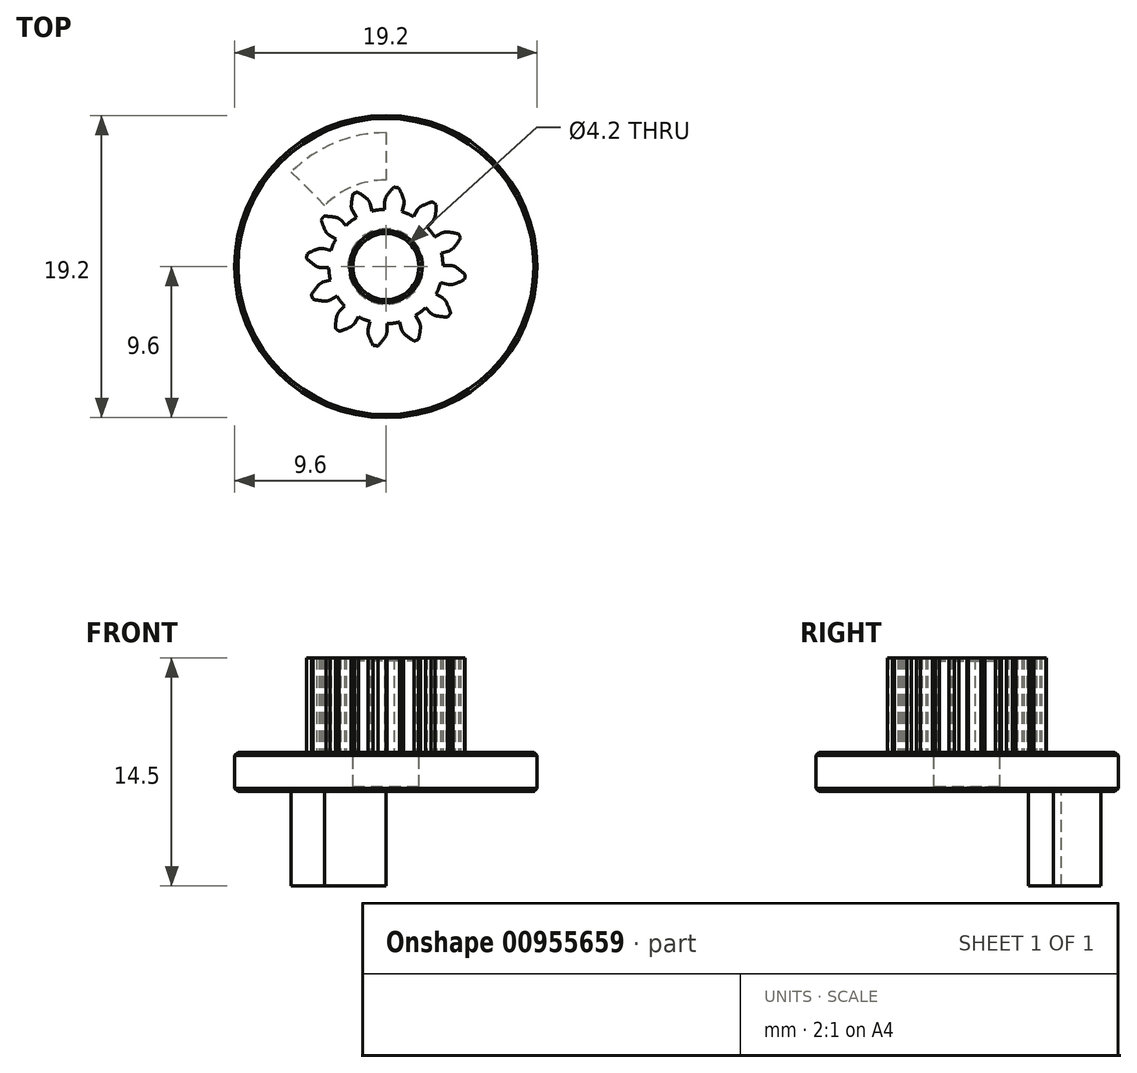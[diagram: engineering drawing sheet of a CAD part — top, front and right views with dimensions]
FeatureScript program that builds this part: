
annotation { "Feature Type Name" : "Feature", "Feature Type Description" : "" }
export const myFeature = defineFeature(function(context is Context, id is Id, definition is map)
    precondition{}
    {
        {
            var Q0;
            Q0=qCreatedBy(makeId("Top.planeOp"),FACE);
            var sketch = newSketch(context, id + "F0", { "sketchPlane" : qUnion([Q0])});
            skCircle(sketch, "E0", {"center": v(0, 0) * mm, "radius": 9.6 * mm});
            skCircle(sketch, "E1", {"center": v(0, 0) * mm, "radius": 2.1 * mm});
            skSolve(sketch);
        }
        {
            var Q0;
            Q0 = qSketchRegion(id + "F0", true);
            extrude(context, id + "F1", {"entities" : qUnion([Q0]), "oppositeDirection" : true, "depth" : 2.5 * mm, "offsetDistance" : 25 * mm});
        }
        {
            var Q0;
            Q0=makeQuery(id+"F1.opExtrude","CAP_FACE",FACE,{"disambiguationData":[OSD([sQuery(id+"F0.wireOp",EDGE,"E0"),sQuery(id+"F0.wireOp",EDGE,"E1")])],"isStart":false});
            var sketch = newSketch(context, id + "F2", { "sketchPlane" : qUnion([Q0])});
            skArc(sketch, "E2", {"start": v(-6.01, -6.01) * mm, "mid": v(-3.25, -7.85) * mm, "end": v(0, -8.5) * mm});
            skArc(sketch, "E3", {"start": v(-3.89, -3.89) * mm, "mid": v(-2.1, -5.08) * mm, "end": v(0, -5.5) * mm});
            skLineSegment(sketch, "E4", {"start": v(0, -8.5) * mm, "end": v(0, -5.5) * mm});
            skLineSegment(sketch, "E5", {"start": v(-6.01, -6.01) * mm, "end": v(-3.89, -3.89) * mm});
            skSolve(sketch);
        }
        {
            var Q0;
            Q0 = qSketchRegion(id + "F2", true);
            extrude(context, id + "F3", {"entities" : qUnion([Q0]), "operationType" : NewBodyOperationType.ADD, "depth" : 6 * mm, "offsetDistance" : 25 * mm});
        }
        {
            var Q0;
            Q0=makeQuery(id+"F1.opExtrude","CAP_FACE",FACE,{"disambiguationData":[OSD([sQuery(id+"F0.wireOp",EDGE,"E0"),sQuery(id+"F0.wireOp",EDGE,"E1")])],"isStart":true});
            var sketch = newSketch(context, id + "F4", { "sketchPlane" : qUnion([Q0])});
            skCircle(sketch, "E6", {"center": v(0, 0) * mm, "radius": 4.4 * mm, "construction": true});
            skLineSegment(sketch, "E7", {"start": v(0, 0) * mm, "end": v(0, 9.6) * mm, "construction": true});
            skLineSegment(sketch, "E8", {"start": v(-3.58, 4.4) * mm, "end": v(3.94, 4.4) * mm, "construction": true});
            skPoint(sketch, "E9", {"position": v(0, 4.4) * mm});
            skLineSegment(sketch, "E10", {"start": v(-4.04, 2.93) * mm, "end": v(3.69, 5.74) * mm, "construction": true});
            skLineSegment(sketch, "E11", {"start": v(0, 0) * mm, "end": v(-1.41, 3.89) * mm, "construction": true});
            skCircle(sketch, "E12", {"center": v(0, 0) * mm, "radius": 4.13 * mm, "construction": true});
            skArc(sketch, "E13", {"start": v(-3.93, 3.2) * mm, "mid": v(-4.02, 3.08) * mm, "end": v(-4.1, 2.96) * mm});
            skCircle(sketch, "E14", {"center": v(0, 0) * mm, "radius": 3.63 * mm});
            skPoint(sketch, "E15", {"position": v(3.58, 2.06) * mm});
            skPoint(sketch, "E16", {"position": v(1.64, 3.8) * mm});
            skArc(sketch, "E17", {"start": v(0, 4.4) * mm, "mid": v(0.24, 4.73) * mm, "end": v(0.51, 5.04) * mm});
            skArc(sketch, "E18", {"start": v(0, 4.4) * mm, "mid": v(-0.04, 4.27) * mm, "end": v(-0.07, 4.13) * mm});
            skLineSegment(sketch, "E19", {"start": v(-0.07, 4.13) * mm, "end": v(-0.07, 3.63) * mm});
            skLineSegment(sketch, "E20", {"start": v(0, 0) * mm, "end": v(0.83, 6.34) * mm, "construction": true});
            skLineSegment(sketch, "E21.MirrorCS", {"start": v(1.14, 3.97) * mm, "end": v(1.01, 3.48) * mm});
            skArc(sketch, "E22.MirrorCS", {"start": v(1.14, 4.25) * mm, "mid": v(1.15, 4.11) * mm, "end": v(1.14, 3.97) * mm});
            skArc(sketch, "E23.MirrorCS", {"start": v(1.14, 4.25) * mm, "mid": v(1, 4.63) * mm, "end": v(0.81, 5) * mm});
            skArc(sketch, "E24.1.0", {"start": v(-2.2, 3.81) * mm, "mid": v(-2.16, 4.22) * mm, "end": v(-2.08, 4.62) * mm});
            skArc(sketch, "E24.1.1", {"start": v(-2.2, 3.81) * mm, "mid": v(-2.17, 3.68) * mm, "end": v(-2.13, 3.54) * mm});
            skLineSegment(sketch, "E24.1.2", {"start": v(-2.13, 3.54) * mm, "end": v(-1.88, 3.1) * mm});
            skLineSegment(sketch, "E24.1.3", {"start": v(-1, 4.01) * mm, "end": v(-0.87, 3.52) * mm});
            skArc(sketch, "E24.1.4", {"start": v(-1.14, 4.25) * mm, "mid": v(-1.06, 4.13) * mm, "end": v(-1, 4.01) * mm});
            skArc(sketch, "E24.1.5", {"start": v(-1.14, 4.25) * mm, "mid": v(-1.46, 4.5) * mm, "end": v(-1.8, 4.74) * mm});
            skArc(sketch, "E24.2.0", {"start": v(-3.81, 2.2) * mm, "mid": v(-3.98, 2.57) * mm, "end": v(-4.1, 2.96) * mm});
            skArc(sketch, "E24.2.1", {"start": v(-3.81, 2.2) * mm, "mid": v(-3.72, 2.1) * mm, "end": v(-3.62, 2) * mm});
            skLineSegment(sketch, "E24.2.2", {"start": v(-3.62, 2) * mm, "end": v(-3.18, 1.75) * mm});
            skLineSegment(sketch, "E24.2.3", {"start": v(-2.87, 2.98) * mm, "end": v(-2.51, 2.62) * mm});
            skArc(sketch, "E24.2.4", {"start": v(-3.11, 3.11) * mm, "mid": v(-2.99, 3.05) * mm, "end": v(-2.87, 2.98) * mm});
            skArc(sketch, "E24.2.5", {"start": v(-3.11, 3.11) * mm, "mid": v(-3.52, 3.18) * mm, "end": v(-3.93, 3.2) * mm});
            skArc(sketch, "E24.3.0", {"start": v(-4.4, 0) * mm, "mid": v(-4.73, 0.24) * mm, "end": v(-5.04, 0.51) * mm});
            skArc(sketch, "E24.3.1", {"start": v(-4.4, 0) * mm, "mid": v(-4.27, -0.04) * mm, "end": v(-4.13, -0.07) * mm});
            skLineSegment(sketch, "E24.3.2", {"start": v(-4.13, -0.07) * mm, "end": v(-3.63, -0.07) * mm});
            skLineSegment(sketch, "E24.3.3", {"start": v(-3.97, 1.14) * mm, "end": v(-3.48, 1.01) * mm});
            skArc(sketch, "E24.3.4", {"start": v(-4.25, 1.14) * mm, "mid": v(-4.11, 1.15) * mm, "end": v(-3.97, 1.14) * mm});
            skArc(sketch, "E24.3.5", {"start": v(-4.25, 1.14) * mm, "mid": v(-4.63, 1) * mm, "end": v(-5, 0.81) * mm});
            skArc(sketch, "E24.4.0", {"start": v(-3.81, -2.2) * mm, "mid": v(-4.22, -2.16) * mm, "end": v(-4.62, -2.08) * mm});
            skArc(sketch, "E24.4.1", {"start": v(-3.81, -2.2) * mm, "mid": v(-3.68, -2.17) * mm, "end": v(-3.54, -2.13) * mm});
            skLineSegment(sketch, "E24.4.2", {"start": v(-3.54, -2.13) * mm, "end": v(-3.1, -1.88) * mm});
            skLineSegment(sketch, "E24.4.3", {"start": v(-4.01, -1) * mm, "end": v(-3.52, -0.87) * mm});
            skArc(sketch, "E24.4.4", {"start": v(-4.25, -1.14) * mm, "mid": v(-4.13, -1.06) * mm, "end": v(-4.01, -1) * mm});
            skArc(sketch, "E24.4.5", {"start": v(-4.25, -1.14) * mm, "mid": v(-4.5, -1.46) * mm, "end": v(-4.74, -1.8) * mm});
            skArc(sketch, "E24.5.0", {"start": v(-2.2, -3.81) * mm, "mid": v(-2.57, -3.98) * mm, "end": v(-2.96, -4.1) * mm});
            skArc(sketch, "E24.5.1", {"start": v(-2.2, -3.81) * mm, "mid": v(-2.1, -3.72) * mm, "end": v(-2, -3.62) * mm});
            skLineSegment(sketch, "E24.5.2", {"start": v(-2, -3.62) * mm, "end": v(-1.75, -3.18) * mm});
            skLineSegment(sketch, "E24.5.3", {"start": v(-2.98, -2.87) * mm, "end": v(-2.62, -2.51) * mm});
            skArc(sketch, "E24.5.4", {"start": v(-3.11, -3.11) * mm, "mid": v(-3.05, -2.99) * mm, "end": v(-2.98, -2.87) * mm});
            skArc(sketch, "E24.5.5", {"start": v(-3.11, -3.11) * mm, "mid": v(-3.18, -3.52) * mm, "end": v(-3.2, -3.93) * mm});
            skArc(sketch, "E24.6.0", {"start": v(0, -4.4) * mm, "mid": v(-0.24, -4.73) * mm, "end": v(-0.51, -5.04) * mm});
            skArc(sketch, "E24.6.1", {"start": v(0, -4.4) * mm, "mid": v(0.04, -4.27) * mm, "end": v(0.07, -4.13) * mm});
            skLineSegment(sketch, "E24.6.2", {"start": v(0.07, -4.13) * mm, "end": v(0.07, -3.63) * mm});
            skLineSegment(sketch, "E24.6.3", {"start": v(-1.14, -3.97) * mm, "end": v(-1.01, -3.48) * mm});
            skArc(sketch, "E24.6.4", {"start": v(-1.14, -4.25) * mm, "mid": v(-1.15, -4.11) * mm, "end": v(-1.14, -3.97) * mm});
            skArc(sketch, "E24.6.5", {"start": v(-1.14, -4.25) * mm, "mid": v(-1, -4.63) * mm, "end": v(-0.81, -5) * mm});
            skArc(sketch, "E24.7.0", {"start": v(2.2, -3.81) * mm, "mid": v(2.16, -4.22) * mm, "end": v(2.08, -4.62) * mm});
            skArc(sketch, "E24.7.1", {"start": v(2.2, -3.81) * mm, "mid": v(2.17, -3.68) * mm, "end": v(2.13, -3.54) * mm});
            skLineSegment(sketch, "E24.7.2", {"start": v(2.13, -3.54) * mm, "end": v(1.88, -3.1) * mm});
            skLineSegment(sketch, "E24.7.3", {"start": v(1, -4.01) * mm, "end": v(0.87, -3.52) * mm});
            skArc(sketch, "E24.7.4", {"start": v(1.14, -4.25) * mm, "mid": v(1.06, -4.13) * mm, "end": v(1, -4.01) * mm});
            skArc(sketch, "E24.7.5", {"start": v(1.14, -4.25) * mm, "mid": v(1.46, -4.5) * mm, "end": v(1.8, -4.74) * mm});
            skArc(sketch, "E24.8.0", {"start": v(3.81, -2.2) * mm, "mid": v(3.98, -2.57) * mm, "end": v(4.1, -2.96) * mm});
            skArc(sketch, "E24.8.1", {"start": v(3.81, -2.2) * mm, "mid": v(3.72, -2.1) * mm, "end": v(3.62, -2) * mm});
            skLineSegment(sketch, "E24.8.2", {"start": v(3.62, -2) * mm, "end": v(3.18, -1.75) * mm});
            skLineSegment(sketch, "E24.8.3", {"start": v(2.87, -2.98) * mm, "end": v(2.51, -2.62) * mm});
            skArc(sketch, "E24.8.4", {"start": v(3.11, -3.11) * mm, "mid": v(2.99, -3.05) * mm, "end": v(2.87, -2.98) * mm});
            skArc(sketch, "E24.8.5", {"start": v(3.11, -3.11) * mm, "mid": v(3.52, -3.18) * mm, "end": v(3.93, -3.2) * mm});
            skArc(sketch, "E24.9.0", {"start": v(4.4, 0) * mm, "mid": v(4.73, -0.24) * mm, "end": v(5.04, -0.51) * mm});
            skArc(sketch, "E24.9.1", {"start": v(4.4, 0) * mm, "mid": v(4.27, 0.04) * mm, "end": v(4.13, 0.07) * mm});
            skLineSegment(sketch, "E24.9.2", {"start": v(4.13, 0.07) * mm, "end": v(3.63, 0.07) * mm});
            skLineSegment(sketch, "E24.9.3", {"start": v(3.97, -1.14) * mm, "end": v(3.48, -1.01) * mm});
            skArc(sketch, "E24.9.4", {"start": v(4.25, -1.14) * mm, "mid": v(4.11, -1.15) * mm, "end": v(3.97, -1.14) * mm});
            skArc(sketch, "E24.9.5", {"start": v(4.25, -1.14) * mm, "mid": v(4.63, -1) * mm, "end": v(5, -0.81) * mm});
            skArc(sketch, "E24.10.0", {"start": v(3.81, 2.2) * mm, "mid": v(4.22, 2.16) * mm, "end": v(4.62, 2.08) * mm});
            skArc(sketch, "E24.10.1", {"start": v(3.81, 2.2) * mm, "mid": v(3.68, 2.17) * mm, "end": v(3.54, 2.13) * mm});
            skLineSegment(sketch, "E24.10.2", {"start": v(3.54, 2.13) * mm, "end": v(3.1, 1.88) * mm});
            skLineSegment(sketch, "E24.10.3", {"start": v(4.01, 1) * mm, "end": v(3.52, 0.87) * mm});
            skArc(sketch, "E24.10.4", {"start": v(4.25, 1.14) * mm, "mid": v(4.13, 1.06) * mm, "end": v(4.01, 1) * mm});
            skArc(sketch, "E24.10.5", {"start": v(4.25, 1.14) * mm, "mid": v(4.5, 1.46) * mm, "end": v(4.74, 1.8) * mm});
            skArc(sketch, "E24.11.0", {"start": v(2.2, 3.81) * mm, "mid": v(2.57, 3.98) * mm, "end": v(2.96, 4.1) * mm});
            skArc(sketch, "E24.11.1", {"start": v(2.2, 3.81) * mm, "mid": v(2.1, 3.72) * mm, "end": v(2, 3.62) * mm});
            skLineSegment(sketch, "E24.11.2", {"start": v(2, 3.62) * mm, "end": v(1.75, 3.18) * mm});
            skLineSegment(sketch, "E24.11.3", {"start": v(2.98, 2.87) * mm, "end": v(2.62, 2.51) * mm});
            skArc(sketch, "E24.11.4", {"start": v(3.11, 3.11) * mm, "mid": v(3.05, 2.99) * mm, "end": v(2.98, 2.87) * mm});
            skArc(sketch, "E24.11.5", {"start": v(3.11, 3.11) * mm, "mid": v(3.18, 3.52) * mm, "end": v(3.2, 3.93) * mm});
            skArc(sketch, "E25.trimOffspring", {"start": v(-5, 0.81) * mm, "mid": v(-5.02, 0.66) * mm, "end": v(-5.04, 0.51) * mm});
            skArc(sketch, "E26.trimOffspring", {"start": v(-4.74, -1.8) * mm, "mid": v(-4.68, -1.94) * mm, "end": v(-4.62, -2.08) * mm});
            skArc(sketch, "E27.trimOffspring", {"start": v(-3.2, -3.93) * mm, "mid": v(-3.08, -4.02) * mm, "end": v(-2.96, -4.1) * mm});
            skArc(sketch, "E28.trimOffspring", {"start": v(-0.81, -5) * mm, "mid": v(-0.66, -5.02) * mm, "end": v(-0.51, -5.04) * mm});
            skArc(sketch, "E29.trimOffspring", {"start": v(1.8, -4.74) * mm, "mid": v(1.94, -4.68) * mm, "end": v(2.08, -4.62) * mm});
            skArc(sketch, "E30.trimOffspring", {"start": v(3.93, -3.2) * mm, "mid": v(4.02, -3.08) * mm, "end": v(4.1, -2.96) * mm});
            skArc(sketch, "E31.trimOffspring", {"start": v(5, -0.81) * mm, "mid": v(5.02, -0.66) * mm, "end": v(5.04, -0.51) * mm});
            skArc(sketch, "E32.trimOffspring", {"start": v(4.74, 1.8) * mm, "mid": v(4.68, 1.94) * mm, "end": v(4.62, 2.08) * mm});
            skArc(sketch, "E33.trimOffspring", {"start": v(3.2, 3.93) * mm, "mid": v(3.08, 4.02) * mm, "end": v(2.96, 4.1) * mm});
            skArc(sketch, "E34.trimOffspring", {"start": v(0.81, 5) * mm, "mid": v(0.66, 5.02) * mm, "end": v(0.51, 5.04) * mm});
            skArc(sketch, "E35.trimOffspring", {"start": v(-1.8, 4.74) * mm, "mid": v(-1.94, 4.68) * mm, "end": v(-2.08, 4.62) * mm});
            skCircle(sketch, "E36", {"center": v(0, 0) * mm, "radius": 2.1 * mm});
            skSolve(sketch);
        }
        {
            var Q0;
            Q0 = qSketchRegion(id + "F4", true);
            extrude(context, id + "F5", {"entities" : qUnion([Q0]), "operationType" : NewBodyOperationType.ADD, "depth" : 6 * mm, "offsetDistance" : 25 * mm});
        }
        {
            var Q0;
            Q0=makeQuery(id+"F1.opExtrude","CAP_EDGE",EDGE,{"disambiguationData":[OSD([sQuery(id+"F0.wireOp",EDGE,"E1")])],"isStart":false});
            chamfer(context, id + "F6", {"entities" : qUnion([Q0]), "width" : .3 * mm, "tangentPropagation" : true});
        }
        {
            var Q0;
            Q0=makeQuery(id+"F5.opExtrude","CAP_EDGE",EDGE,{"disambiguationData":[OSD([sQuery(id+"F4.wireOp",EDGE,"E36")])],"isStart":false});
            chamfer(context, id + "F7", {"entities" : qUnion([Q0]), "width" : .2 * mm, "tangentPropagation" : true});
        }
        {
            var Q0;
            Q0=makeQuery(id+"F1.opExtrude","CAP_EDGE",EDGE,{"disambiguationData":[OSD([sQuery(id+"F0.wireOp",EDGE,"E0")])],"isStart":false});
            var Q1;
            Q1=makeQuery(id+"F1.opExtrude","CAP_EDGE",EDGE,{"disambiguationData":[OSD([sQuery(id+"F0.wireOp",EDGE,"E0")])],"isStart":true});
            chamfer(context, id + "F8", {"entities" : qUnion([Q0, Q1]), "width" : .2 * mm, "tangentPropagation" : true});
        }
    });
